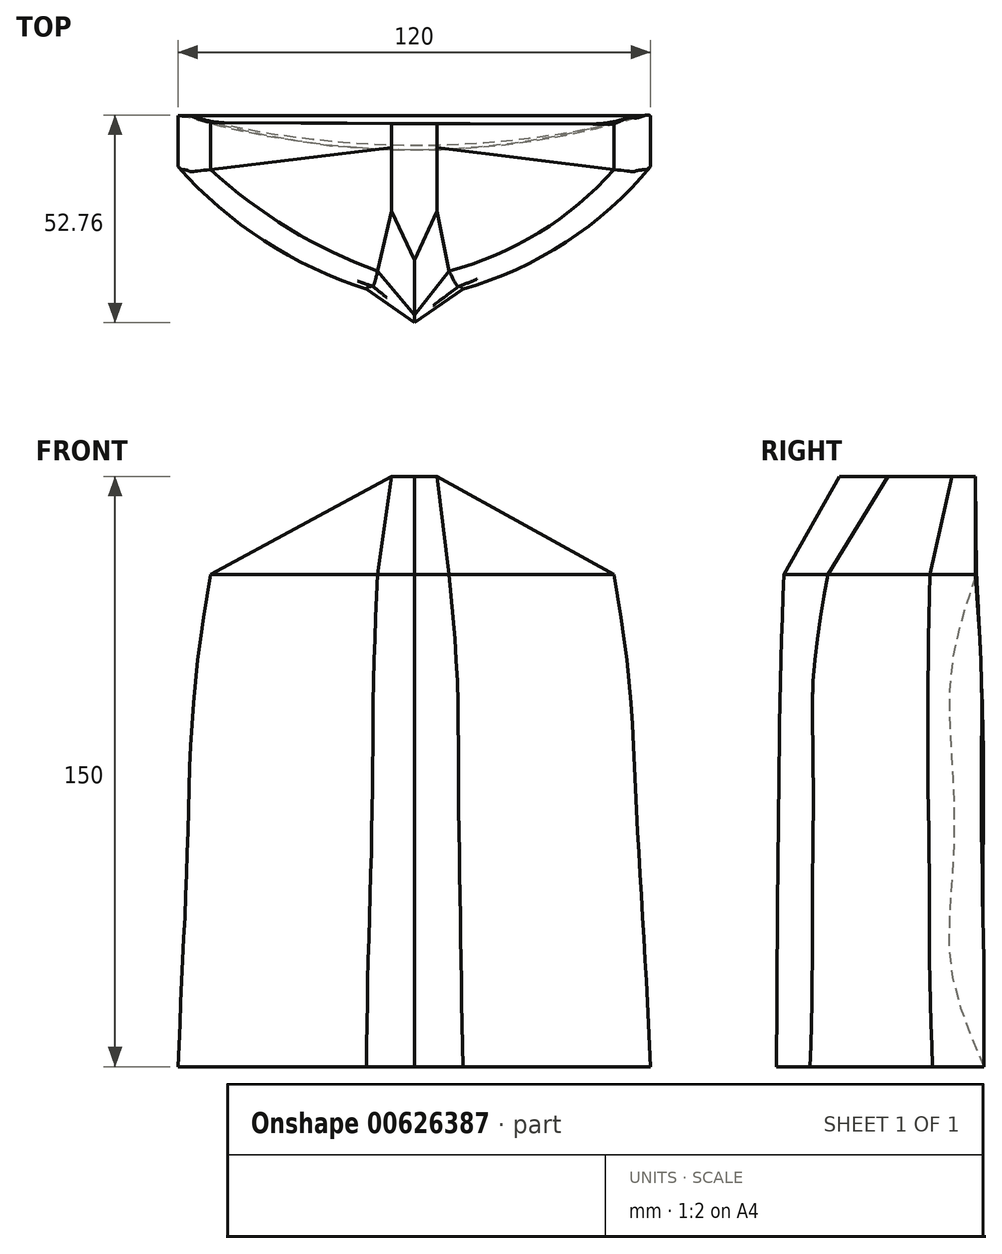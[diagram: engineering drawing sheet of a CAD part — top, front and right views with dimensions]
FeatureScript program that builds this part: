
annotation { "Feature Type Name" : "Feature", "Feature Type Description" : "" }
export const myFeature = defineFeature(function(context is Context, id is Id, definition is map)
    precondition{}
    {
        {
            var Q0;
            Q0=qCreatedBy(makeId("Top.planeOp"),FACE);
            var sketch = newSketch(context, id + "F0", { "sketchPlane" : qUnion([Q0])});
            skLineSegment(sketch, "E0", {"start": v(0, 0) * mm, "end": v(12.33, 8.57) * mm});
            skLineSegment(sketch, "E1", {"start": v(0, 0) * mm, "end": v(-12.15, 8.57) * mm});
            skLineSegment(sketch, "E2", {"start": v(-60, 52.66) * mm, "end": v(-60, 39.66) * mm});
            skLineSegment(sketch, "E3", {"start": v(60, 52.66) * mm, "end": v(60, 39.66) * mm});
            skPoint(sketch, "E4.start.orphan", {"position": v(0, 52.66) * mm});
            skArc(sketch, "E5", {"start": v(-60, 39.66) * mm, "mid": v(-38.19, 20.86) * mm, "end": v(-12.15, 8.57) * mm});
            skArc(sketch, "E6", {"start": v(12.33, 8.57) * mm, "mid": v(38.54, 20.47) * mm, "end": v(60, 39.66) * mm});
            skLineSegment(sketch, "E7", {"start": v(-60, 52.66) * mm, "end": v(60, 52.66) * mm});
            skSolve(sketch);
        }
        {
            var Q0;
            Q0=qCreatedBy(makeId("Top.planeOp"),FACE);
            cPlane(context, id + "F1", {"entities" : qUnion([Q0]), "cplaneType" : CPlaneType.OFFSET, "offset" : 25 * mm, "width" : 150 * mm, "height" : 150 * mm});
        }
        {
            var Q0;
            Q0=qCreatedBy(id+"F1.planeOp",FACE);
            var sketch = newSketch(context, id + "F2", { "sketchPlane" : qUnion([Q0])});
            skLineSegment(sketch, "E8", {"start": v(-58.93, 52.55) * mm, "end": v(-58.93, 38.92) * mm});
            skLineSegment(sketch, "E9", {"start": v(58.8, 52.72) * mm, "end": v(58.8, 38.92) * mm});
            skArc(sketch, "E10", {"start": v(-58.93, 52.55) * mm, "mid": v(-0.06, 44.32) * mm, "end": v(58.8, 52.72) * mm});
            skPoint(sketch, "E11.start.orphan", {"position": v(0, 1.78) * mm});
            skPoint(sketch, "E12.start.orphan", {"position": v(11.6, 9.96) * mm});
            skPoint(sketch, "E13.end.orphan", {"position": v(-11.06, 9.96) * mm});
            skLineSegment(sketch, "E14", {"start": v(-11.76, 9.07) * mm, "end": v(0, 0.18) * mm});
            skLineSegment(sketch, "E15", {"start": v(0, 0.18) * mm, "end": v(11.9, 9.12) * mm});
            skArc(sketch, "E16", {"start": v(11.9, 9.12) * mm, "mid": v(37.33, 20.89) * mm, "end": v(58.8, 38.92) * mm});
            skArc(sketch, "E17", {"start": v(-58.93, 38.92) * mm, "mid": v(-37.27, 20.96) * mm, "end": v(-11.76, 9.07) * mm});
            skSolve(sketch);
        }
        {
            var Q0;
            Q0=qCreatedBy(id+"F1.planeOp",FACE);
            cPlane(context, id + "F3", {"entities" : qUnion([Q0]), "cplaneType" : CPlaneType.OFFSET, "offset" : 25 * mm, "width" : 150 * mm, "height" : 150 * mm});
        }
        {
            var Q0;
            Q0=qCreatedBy(id+"F3.planeOp",FACE);
            var sketch = newSketch(context, id + "F4", { "sketchPlane" : qUnion([Q0])});
            skLineSegment(sketch, "E18", {"start": v(-57.8, 52.48) * mm, "end": v(-57.8, 38.82) * mm});
            skLineSegment(sketch, "E19", {"start": v(57.3, 52.25) * mm, "end": v(57.3, 38.82) * mm});
            skArc(sketch, "E20", {"start": v(-57.8, 52.48) * mm, "mid": v(-0.27, 44.77) * mm, "end": v(57.3, 52.25) * mm});
            skLineSegment(sketch, "E21", {"start": v(0, 0.38) * mm, "end": v(11.52, 9.22) * mm});
            skLineSegment(sketch, "E22", {"start": v(0, 0.38) * mm, "end": v(-11.03, 9.22) * mm});
            skArc(sketch, "E23", {"start": v(-57.8, 38.82) * mm, "mid": v(-36.36, 20.95) * mm, "end": v(-11.03, 9.22) * mm});
            skArc(sketch, "E24", {"start": v(11.52, 9.22) * mm, "mid": v(36.18, 21.29) * mm, "end": v(57.3, 38.82) * mm});
            skPoint(sketch, "E25.orphan", {"position": v(6.9, 123.17) * mm});
            skPoint(sketch, "E26.end.orphan", {"position": v(6.9, 117.87) * mm});
            skPoint(sketch, "E27.start.orphan", {"position": v(0, 75.63) * mm});
            skSolve(sketch);
        }
        {
            var Q0;
            Q0=qCreatedBy(id+"F3.planeOp",FACE);
            cPlane(context, id + "F5", {"entities" : qUnion([Q0]), "cplaneType" : CPlaneType.OFFSET, "offset" : 25 * mm, "width" : 150 * mm, "height" : 150 * mm});
        }
        {
            var Q0;
            Q0=qCreatedBy(id+"F5.planeOp",FACE);
            var sketch = newSketch(context, id + "F6", { "sketchPlane" : qUnion([Q0])});
            skLineSegment(sketch, "E28", {"start": v(0, 0.66) * mm, "end": v(11.2, 9.33) * mm});
            skLineSegment(sketch, "E29", {"start": v(0, 0.66) * mm, "end": v(-10.59, 9.33) * mm});
            skLineSegment(sketch, "E30", {"start": v(56, 52.06) * mm, "end": v(56, 38.48) * mm});
            skLineSegment(sketch, "E31", {"start": v(-57.08, 38.48) * mm, "end": v(-57.08, 52.6) * mm});
            skArc(sketch, "E32", {"start": v(-57.08, 38.48) * mm, "mid": v(-35.7, 20.93) * mm, "end": v(-10.59, 9.33) * mm});
            skArc(sketch, "E33", {"start": v(11.2, 9.33) * mm, "mid": v(35.39, 21.16) * mm, "end": v(56, 38.48) * mm});
            skArc(sketch, "E34", {"start": v(-57.08, 52.6) * mm, "mid": v(-0.57, 44.75) * mm, "end": v(56, 52.06) * mm});
            skSolve(sketch);
        }
        {
            var Q0;
            Q0=qCreatedBy(id+"F5.planeOp",FACE);
            cPlane(context, id + "F7", {"entities" : qUnion([Q0]), "cplaneType" : CPlaneType.OFFSET, "offset" : 25 * mm, "width" : 150 * mm, "height" : 150 * mm});
        }
        {
            var Q0;
            Q0=qCreatedBy(id+"F7.planeOp",FACE);
            var sketch = newSketch(context, id + "F8", { "sketchPlane" : qUnion([Q0])});
            skLineSegment(sketch, "E35", {"start": v(-55.4, 52.04) * mm, "end": v(-55.4, 38.54) * mm});
            skLineSegment(sketch, "E36", {"start": v(54.36, 52.04) * mm, "end": v(54.36, 38.54) * mm});
            skLineSegment(sketch, "E37", {"start": v(0, 1.06) * mm, "end": v(10.83, 9.46) * mm});
            skLineSegment(sketch, "E38", {"start": v(0, 1.06) * mm, "end": v(-10.29, 9.6) * mm});
            skArc(sketch, "E39", {"start": v(-55.4, 38.54) * mm, "mid": v(-34.34, 21.75) * mm, "end": v(-10.29, 9.6) * mm});
            skArc(sketch, "E40", {"start": v(10.83, 9.46) * mm, "mid": v(33.93, 22) * mm, "end": v(54.36, 38.54) * mm});
            skArc(sketch, "E41", {"start": v(-55.4, 52.04) * mm, "mid": v(-0.52, 44.25) * mm, "end": v(54.36, 52.04) * mm});
            skSolve(sketch);
        }
        {
            var Q0;
            Q0=qCreatedBy(id+"F7.planeOp",FACE);
            cPlane(context, id + "F9", {"entities" : qUnion([Q0]), "cplaneType" : CPlaneType.OFFSET, "offset" : 25 * mm, "width" : 150 * mm, "height" : 150 * mm});
        }
        {
            var Q0;
            Q0=qCreatedBy(id+"F9.planeOp",FACE);
            var sketch = newSketch(context, id + "F10", { "sketchPlane" : qUnion([Q0])});
            skLineSegment(sketch, "E42", {"start": v(-51.75, 50.87) * mm, "end": v(-51.75, 38.94) * mm});
            skLineSegment(sketch, "E43", {"start": v(0, 1.93) * mm, "end": v(-9.29, 13.11) * mm});
            skLineSegment(sketch, "E44", {"start": v(0, 1.93) * mm, "end": v(8.8, 13.11) * mm});
            skLineSegment(sketch, "E45", {"start": v(50.73, 50.5) * mm, "end": v(50.73, 38.94) * mm});
            skArc(sketch, "E46", {"start": v(-51.75, 38.94) * mm, "mid": v(-31.8, 23.92) * mm, "end": v(-9.29, 13.11) * mm});
            skArc(sketch, "E47", {"start": v(8.8, 13.11) * mm, "mid": v(31.69, 22.91) * mm, "end": v(50.73, 38.94) * mm});
            skLineSegment(sketch, "E48", {"start": v(-51.75, 50.87) * mm, "end": v(50.73, 50.5) * mm});
            skSolve(sketch);
        }
        {
            var Q0;
            Q0=makeQuery(id+"F10.imprint","IMPRINT",FACE,{"disambiguationData":[TD([[makeQuery(id+"F10.imprint","IMPRINT",EDGE,{"derivedFrom":sQuery(id+"F10.wireOp",EDGE,"E42")}),1.0]])]});
            var Q1;
            Q1=makeQuery(id+"F8.imprint","IMPRINT",FACE,{"disambiguationData":[TD([[makeQuery(id+"F8.imprint","IMPRINT",EDGE,{"derivedFrom":sQuery(id+"F8.wireOp",EDGE,"E35")}),1.0]])]});
            var Q2;
            Q2=makeQuery(id+"F6.imprint","IMPRINT",FACE,{"disambiguationData":[TD([[makeQuery(id+"F6.imprint","IMPRINT",EDGE,{"derivedFrom":sQuery(id+"F6.wireOp",EDGE,"E28")}),1.0]])]});
            var Q3;
            Q3=makeQuery(id+"F4.imprint","IMPRINT",FACE,{"disambiguationData":[TD([[makeQuery(id+"F4.imprint","IMPRINT",EDGE,{"derivedFrom":sQuery(id+"F4.wireOp",EDGE,"E18")}),1.0]])]});
            var Q4;
            Q4=makeQuery(id+"F2.imprint","IMPRINT",FACE,{"disambiguationData":[TD([[makeQuery(id+"F2.imprint","IMPRINT",EDGE,{"derivedFrom":sQuery(id+"F2.wireOp",EDGE,"E8")}),1.0]])]});
            var Q5;
            Q5=makeQuery(id+"F0.imprint","IMPRINT",FACE,{"disambiguationData":[TD([[makeQuery(id+"F0.imprint","IMPRINT",EDGE,{"derivedFrom":sQuery(id+"F0.wireOp",EDGE,"E0")}),1.0]])]});
            loft(context, id + "F11", {"sheetProfilesArray" : [{ "sheetProfileEntities" : qUnion([Q0]) }, { "sheetProfileEntities" : qUnion([Q1]) }, { "sheetProfileEntities" : qUnion([Q2]) }, { "sheetProfileEntities" : qUnion([Q3]) }, { "sheetProfileEntities" : qUnion([Q4]) }, { "sheetProfileEntities" : qUnion([Q5]) }]});
        }
        {
            var Q0;
            Q0=qCreatedBy(id+"F9.planeOp",FACE);
            cPlane(context, id + "F12", {"entities" : qUnion([Q0]), "cplaneType" : CPlaneType.OFFSET, "offset" : 25 * mm, "width" : 150 * mm, "height" : 150 * mm});
        }
        {
            var Q0;
            Q0=qCreatedBy(id+"F12.planeOp",FACE);
            var sketch = newSketch(context, id + "F13", { "sketchPlane" : qUnion([Q0])});
            skPoint(sketch, "E49.end.orphan", {"position": v(0, 2.28) * mm});
            skPoint(sketch, "E50.end.orphan", {"position": v(10.96, 50.71) * mm});
            skPoint(sketch, "E51.end.orphan", {"position": v(-9.9, 22.14) * mm});
            skPoint(sketch, "E52.end.orphan", {"position": v(10.96, 22.14) * mm});
            skPoint(sketch, "E53.end.orphan", {"position": v(1.97, 28.35) * mm});
            skLineSegment(sketch, "E54", {"start": v(5.75, 50.56) * mm, "end": v(-5.75, 50.56) * mm});
            skLineSegment(sketch, "E55", {"start": v(-5.75, 28.35) * mm, "end": v(-5.75, 44.56) * mm});
            skLineSegment(sketch, "E56", {"start": v(-5.75, 44.56) * mm, "end": v(-5.75, 50.56) * mm});
            skLineSegment(sketch, "E57", {"start": v(5.75, 28.35) * mm, "end": v(5.75, 44.56) * mm});
            skLineSegment(sketch, "E58", {"start": v(5.75, 44.56) * mm, "end": v(5.75, 50.56) * mm});
            skLineSegment(sketch, "E59", {"start": v(-5.75, 28.35) * mm, "end": v(0, 15.97) * mm});
            skLineSegment(sketch, "E60", {"start": v(0, 15.97) * mm, "end": v(5.75, 28.35) * mm});
            skSolve(sketch);
        }
        {
            var Q1;
            Q1=makeQuery(id+"F13.imprint","IMPRINT",FACE,{"disambiguationData":[TD([[makeQuery(id+"F13.imprint","IMPRINT",EDGE,{"derivedFrom":sQuery(id+"F13.wireOp",EDGE,"E54")}),1.0]])]});
            var Q2;
            Q2=makeQuery(id+"F11.opLoft","CAP_FACE",FACE,{"disambiguationData":[OSD([makeQuery(id+"F10.imprint","IMPRINT",FACE,{"disambiguationData":[TD([[makeQuery(id+"F10.imprint","IMPRINT",EDGE,{"derivedFrom":sQuery(id+"F10.wireOp",EDGE,"E42")}),1.0]])]})])],"isStart":true});
            loft(context, id + "F14", {"operationType" : NewBodyOperationType.ADD, "sheetProfilesArray" : [{ "sheetProfileEntities" : qUnion([Q1]) }, { "sheetProfileEntities" : qUnion([Q2]) }]});
        }
    });
